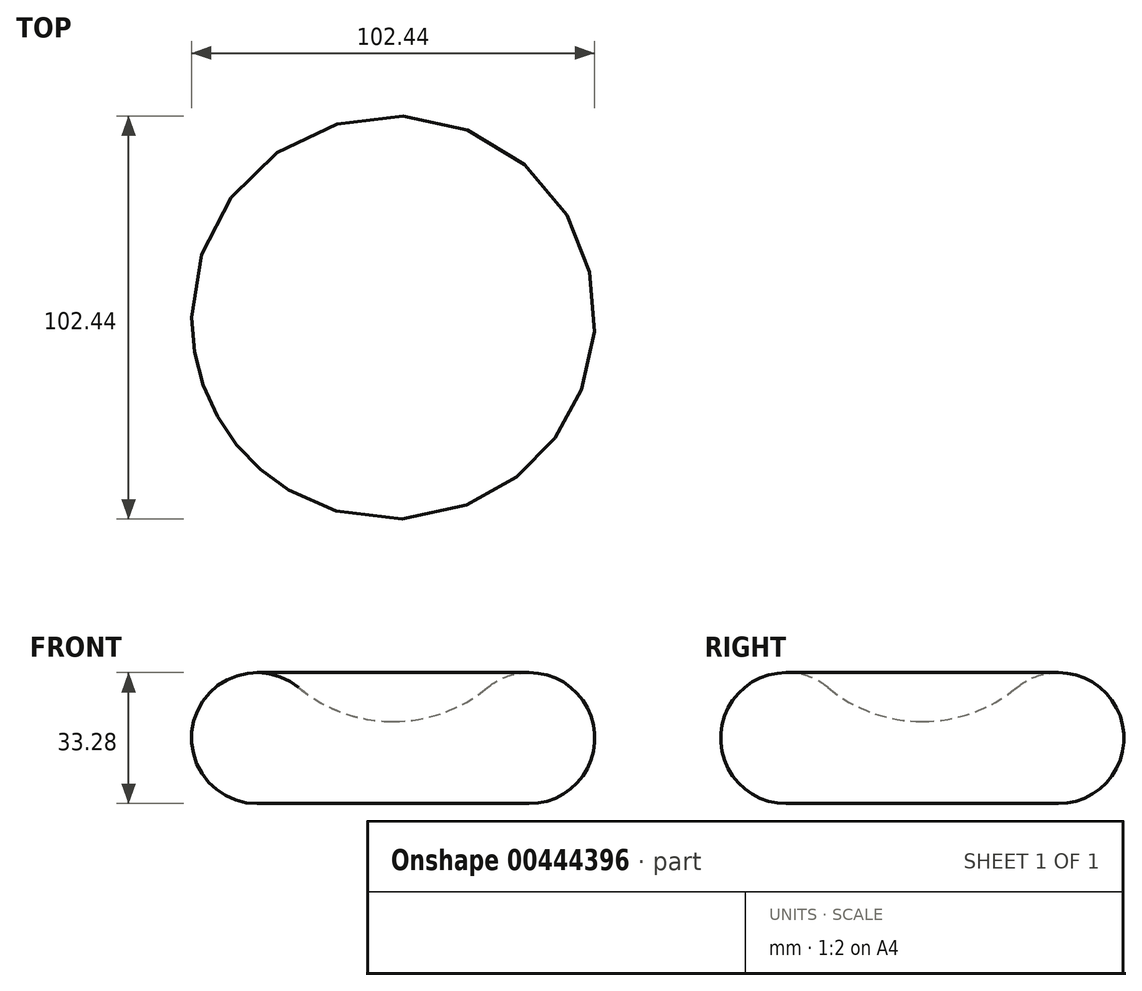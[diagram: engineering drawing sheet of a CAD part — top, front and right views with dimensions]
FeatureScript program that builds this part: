
annotation { "Feature Type Name" : "Feature", "Feature Type Description" : "" }
export const myFeature = defineFeature(function(context is Context, id is Id, definition is map)
    precondition{}
    {
        {
            var Q0;
            Q0=qCreatedBy(makeId("Front.planeOp"),FACE);
            var sketch = newSketch(context, id + "F0", { "sketchPlane" : qUnion([Q0])});
            skArc(sketch, "E0", {"start": v(-23.97, -28.97) * mm, "mid": v(-12.74, -35.37) * mm, "end": v(0, -37.6) * mm});
            skArc(sketch, "E1", {"start": v(-23.97, -28.97) * mm, "mid": v(-50.24, -36.15) * mm, "end": v(-34.58, -58.43) * mm});
            skLineSegment(sketch, "E2", {"start": v(-34.58, -58.43) * mm, "end": v(0, -58.43) * mm});
            skLineSegment(sketch, "E3", {"start": v(0, -58.43) * mm, "end": v(0, -37.6) * mm});
            skSolve(sketch);
        }
        {
            var Q0;
            Q0=makeQuery(id+"F0.imprint","IMPRINT",FACE,{"disambiguationData":[TD([[makeQuery(id+"F0.imprint","IMPRINT",EDGE,{"derivedFrom":sQuery(id+"F0.wireOp",EDGE,"E0")}),-1.0]])]});
            var Q1;
            Q1=sQuery(id+"F0.wireOp",EDGE,"E3");
            revolve(context, id + "F1", {"entities" : qUnion([Q0]), "axis" : qUnion([Q1]), "revolveType" : RevolveType.FULL});
        }
    });
